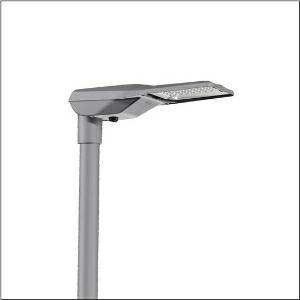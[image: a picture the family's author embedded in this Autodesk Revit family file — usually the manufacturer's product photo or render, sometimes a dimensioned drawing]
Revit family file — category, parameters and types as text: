
# Revit family: streetlight_sl_21_mini___p0_8ab_5xe2r33r08gb_1b3d
name_source: partatom
category: Lighting Fixtures
units: mm (PartAtom-declared; Revit-internal decimal feet)

## family parameters
Cut with Voids When Loaded = No
Host = Face
Light Source = No
Part Type = Normal
Room Calculation Point = No
Round Connector Dimension = Use Diameter
Shared = No

## types (1)
- --- (1 x LED, 5160 lm, 40.4 W, 3000K)
    Apparent Load = 40 VA
    CIE Flux Codes = 36 71 98 100 100
    Color Rendering = 70
    Color Temperature = 3000K
    Default Elevation = 1800 mm
    Description = Streetlight SL 21 mini, mast luminaire, primary light control with lens, of PMMA, primary optical cover: cover, of toughened safety glass, transparent, light distribution: P0.8aB, light emission: direct distribution, primary light characteristic: asymmetric, installation type: post-top, side-entry, LED, High Power LED, rated luminous flux: 5.160lm, luminous efficacy: 128lm/W, light colour: 730, colour temperature: 3000K, control gear: D4i, control: pre-setting: logarithmic dimming characteristic, flexible luminous flux parameterisation, time-dependent luminous flux control, constant luminous flux control, overheat protection, mains connection: 220..240V, AC, 50/60Hz, start of lifetime: 40W, end of service life: 41W, reduction: 19W, luminaire housing, of diecast aluminium, powder-coated, Siteco® metallic grey (DB 702S), corrosivity category C5 mid according to DIN EN ISO 12944, multi-level sealing system, sealing non-destructively replaceable, inclination adjustable: 0°, 5°, 10°, 15°, please order mast flange separately, length: 628mm, width: 235mm, height: 110mm, mast flange for spigot size: 42mm (side-entry): 5XC10008XM4, 60/48mm (side-entry/post-top): 5XC10108XM2, 76/60mm (side-entry/post-top): 5XC10108XM1, mounting height: 4..8m, Smart Interface below, protection rating (complete): IP66, insulation class (complete): insulation class II (safety insulation), certification: CE, ENEC, ENEC+, VDE, impact resistance: IK09, permissible operating ambient temperature for outdoor applications: -40..+50°C, standard-compliant lighting for roads and squares, packaging unit: 1 piece

Light Distribution: P0.8aB
    Height = 110 mm
    Lamp = 1 x LED
    Lamp Light Flux = 5160 lm
    Lamp Power = 40.4 W
    Lamp count = 1
    Length = 625 mm
    Luminous efficacy = 128 lm/W
    Manufacturer = Siteco
    ModVariant = No
    Model = 5XE2R33R08GB
    Number of Poles = 1
    OnlyDefault = Yes
    Power Factor = 1
    Product Name = Streetlight SL 21 mini | P0.8aB
    Product group = mast luminaire | pylon top
    ProductGroupID = 6100
    Protection Class = Protection class II
    Protection Degree = IP 66
    RLX_Detail_Level = 1
    RLX_Emergency_Light_Flux = 0 lm
    RLX_Emergency_Type = 0
    RLX_Emergency_Type_DB = No
    RlxData = <blob elided: 93089 chars, md5=e5e68b17>
    Socket = socket
    Standby Power = 0 W
    System Light Flux = 5160 lm
    System Power = 40 W
    Type Comments = factory setting: luminous flux: 100 % | dim-lin: 254 | 812 mA
    Type Image = l_1003516.jpg
    URL = http://relux.com
    VarID = @adj_071680
    Voltage = 0 V
    Weight = 0.00 kg
    Width = 234 mm

## geometry (parser evidence)
native form markers: Blend x4, Sweep x12
no freeform markers — native parametric forms only
